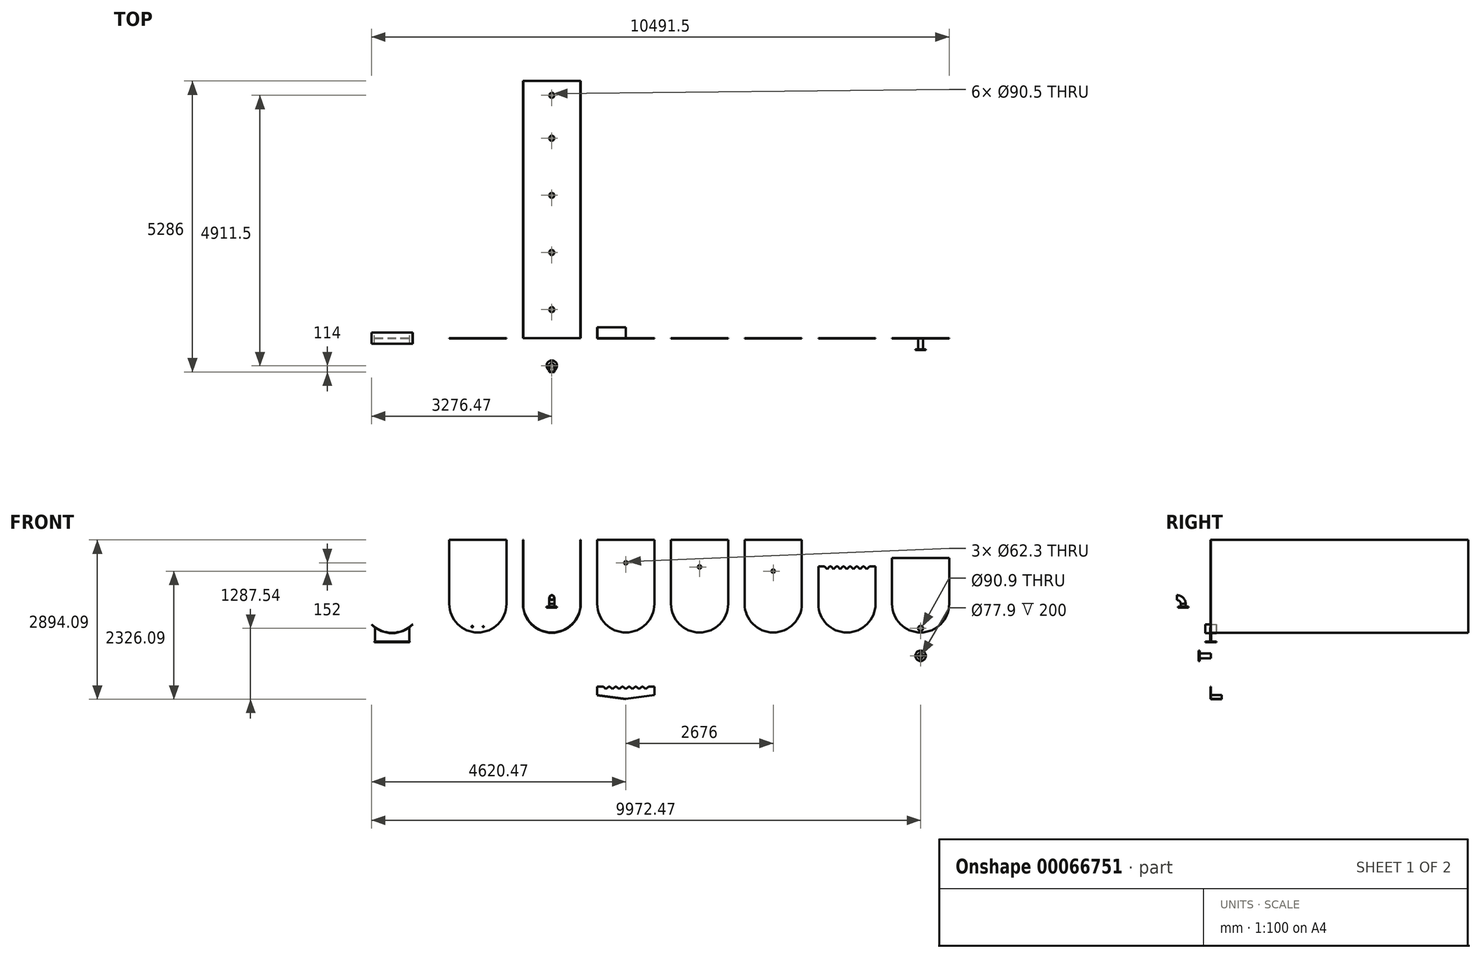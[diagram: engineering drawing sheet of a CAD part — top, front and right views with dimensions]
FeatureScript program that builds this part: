
annotation { "Feature Type Name" : "Feature", "Feature Type Description" : "" }
export const myFeature = defineFeature(function(context is Context, id is Id, definition is map)
    precondition{}
    {
        {
            assignVariable(context, id + "F0", {"name" : "A3", "anyValue" : 6});
        }
        {
            assignVariable(context, id + "F1", {"name" : "A20", "anyValue" : 18});
        }
        {
            assignVariable(context, id + "F2", {"name" : "A22", "anyValue" : 4});
        }
        {
            var Q0;
            Q0=qCreatedBy(makeId("Front.planeOp"),FACE);
            var sketch = newSketch(context, id + "F3", { "sketchPlane" : qUnion([Q0])});
            skLineSegment(sketch, "E0", {"start": v(-519, 1163) * mm, "end": v(-519, 0) * mm});
            skLineSegment(sketch, "E1", {"start": v(0, 0) * mm, "end": v(0, 1223.8) * mm, "construction": true});
            skLineSegment(sketch, "E2", {"start": v(-519, 1163) * mm, "end": v(-525, 1163) * mm});
            skLineSegment(sketch, "E3", {"start": v(-525, 1163) * mm, "end": v(-525, 0) * mm});
            skLineSegment(sketch, "E4.MirrorCS", {"start": v(519, 1163) * mm, "end": v(519, 0) * mm});
            skLineSegment(sketch, "E5.MirrorCS", {"start": v(519, 1163) * mm, "end": v(525, 1163) * mm});
            skLineSegment(sketch, "E6.MirrorCS", {"start": v(525, 1163) * mm, "end": v(525, 0) * mm});
            skArc(sketch, "E7", {"start": v(-519, 0) * mm, "mid": v(0, -519) * mm, "end": v(519, 0) * mm});
            skArc(sketch, "E8", {"start": v(-525, 0) * mm, "mid": v(0, -525) * mm, "end": v(525, 0) * mm});
            skLineSegment(sketch, "E9", {"start": v(-525, 1163) * mm, "end": v(-825, 1163) * mm, "construction": true});
            skLineSegment(sketch, "E10", {"start": v(-825, 1163) * mm, "end": v(-825, 0) * mm});
            skLineSegment(sketch, "E11", {"start": v(-825, 1163) * mm, "end": v(-1863, 1163) * mm});
            skLineSegment(sketch, "E12", {"start": v(-1863, 1163) * mm, "end": v(-1863, 0) * mm});
            skArc(sketch, "E13", {"start": v(-1863, 0) * mm, "mid": v(-1344, -519) * mm, "end": v(-825, 0) * mm});
            skLineSegment(sketch, "E14", {"start": v(525, 1163) * mm, "end": v(825, 1163) * mm, "construction": true});
            skLineSegment(sketch, "E15", {"start": v(825, 1163) * mm, "end": v(1863, 1163) * mm});
            skLineSegment(sketch, "E16", {"start": v(1863, 1163) * mm, "end": v(1863, 0) * mm});
            skLineSegment(sketch, "E17", {"start": v(825, 1163) * mm, "end": v(825, 0) * mm});
            skArc(sketch, "E18", {"start": v(825, 0) * mm, "mid": v(1344, -519) * mm, "end": v(1863, 0) * mm});
            skCircle(sketch, "E19", {"center": v(1344, 747) * mm, "radius": 31.15 * mm});
            skLineSegment(sketch, "E20", {"start": v(1863, 1163) * mm, "end": v(2163, 1163) * mm, "construction": true});
            skLineSegment(sketch, "E21", {"start": v(2163, 1163) * mm, "end": v(2163, 0) * mm});
            skLineSegment(sketch, "E22", {"start": v(2163, 1163) * mm, "end": v(3201, 1163) * mm});
            skLineSegment(sketch, "E23", {"start": v(3201, 1163) * mm, "end": v(3201, 0) * mm});
            skLineSegment(sketch, "E24", {"start": v(3201, 1163) * mm, "end": v(3501, 1163) * mm, "construction": true});
            skLineSegment(sketch, "E25", {"start": v(3501, 1163) * mm, "end": v(4539, 1163) * mm});
            skLineSegment(sketch, "E26", {"start": v(4539, 1163) * mm, "end": v(4539, 0) * mm});
            skLineSegment(sketch, "E27", {"start": v(3501, 1163) * mm, "end": v(3501, 0) * mm});
            skLineSegment(sketch, "E28", {"start": v(4539, 1163) * mm, "end": v(4839, 1163) * mm, "construction": true});
            skLineSegment(sketch, "E29", {"start": v(4839, 1163) * mm, "end": v(5877, 1163) * mm, "construction": true});
            skLineSegment(sketch, "E30", {"start": v(4839, 682.3) * mm, "end": v(4839, 0) * mm});
            skLineSegment(sketch, "E31", {"start": v(5877, 682.3) * mm, "end": v(5877, 0) * mm});
            skArc(sketch, "E32", {"start": v(2163, 0) * mm, "mid": v(2682, -519) * mm, "end": v(3201, 0) * mm});
            skArc(sketch, "E33", {"start": v(3501, 0) * mm, "mid": v(4020, -519) * mm, "end": v(4539, 0) * mm});
            skArc(sketch, "E34", {"start": v(4839, 0) * mm, "mid": v(5358, -519) * mm, "end": v(5877, 0) * mm});
            skCircle(sketch, "E35", {"center": v(2682, 671) * mm, "radius": 31.15 * mm});
            skCircle(sketch, "E36", {"center": v(4020, 595) * mm, "radius": 31.15 * mm});
            skCircle(sketch, "E37", {"center": v(5358, 520) * mm, "radius": 31.15 * mm, "construction": true});
            skLineSegment(sketch, "E38", {"start": v(-1863, 0) * mm, "end": v(-2901, 0) * mm, "construction": true});
            skLineSegment(sketch, "E39", {"start": v(-2901, 0) * mm, "end": v(-2901, -681) * mm, "construction": true});
            skLineSegment(sketch, "E40", {"start": v(-2901, 0) * mm, "end": v(-3272.23, -371.23) * mm, "construction": true});
            skArc(sketch, "E41", {"start": v(-3272.23, -371.23) * mm, "mid": v(-2901, -525) * mm, "end": v(-2529.77, -371.23) * mm});
            skArc(sketch, "E42.0", {"start": v(-3276.47, -375.47) * mm, "mid": v(-2901, -531) * mm, "end": v(-2525.53, -375.47) * mm});
            skLineSegment(sketch, "E43", {"start": v(-3272.23, -371.23) * mm, "end": v(-3276.47, -375.47) * mm});
            skLineSegment(sketch, "E44", {"start": v(-2529.77, -371.23) * mm, "end": v(-2525.53, -375.47) * mm});
            skLineSegment(sketch, "E45", {"start": v(-3220.22, -681) * mm, "end": v(-2581.78, -681) * mm});
            skLineSegment(sketch, "E46", {"start": v(-3220.22, -681) * mm, "end": v(-3220.22, -697) * mm});
            skLineSegment(sketch, "E47", {"start": v(-3220.22, -697) * mm, "end": v(-2581.78, -697) * mm});
            skLineSegment(sketch, "E48", {"start": v(-2581.78, -697) * mm, "end": v(-2581.78, -681) * mm});
            skLineSegment(sketch, "E49", {"start": v(-3211.47, -681) * mm, "end": v(-3211.47, -430.77) * mm});
            skLineSegment(sketch, "E50.MirrorCS", {"start": v(-2590.53, -681) * mm, "end": v(-2590.53, -430.77) * mm});
            skPoint(sketch, "E51.endSnap0", {"position": v(0, -519) * mm});
            skLineSegment(sketch, "E52", {"start": v(934, -1500) * mm, "end": v(984, -1550) * mm});
            skLineSegment(sketch, "E53", {"start": v(984, -1550) * mm, "end": v(984, -936.12) * mm, "construction": true});
            skLineSegment(sketch, "E54.MirrorCS", {"start": v(1034, -1500) * mm, "end": v(984, -1550) * mm});
            skLineSegment(sketch, "E55", {"start": v(934, -1500) * mm, "end": v(825, -1500) * mm});
            skLineSegment(sketch, "E56", {"start": v(1034, -1500) * mm, "end": v(1054, -1500) * mm});
            skLineSegment(sketch, "E57.1.0.0", {"start": v(1054, -1500) * mm, "end": v(1104, -1550) * mm});
            skLineSegment(sketch, "E57.1.0.1", {"start": v(1154, -1500) * mm, "end": v(1104, -1550) * mm});
            skLineSegment(sketch, "E57.1.0.2", {"start": v(1154, -1500) * mm, "end": v(1174, -1500) * mm});
            skLineSegment(sketch, "E57.2.0.0", {"start": v(1174, -1500) * mm, "end": v(1224, -1550) * mm});
            skLineSegment(sketch, "E57.2.0.1", {"start": v(1274, -1500) * mm, "end": v(1224, -1550) * mm});
            skLineSegment(sketch, "E57.2.0.2", {"start": v(1274, -1500) * mm, "end": v(1294, -1500) * mm});
            skLineSegment(sketch, "E57.3.0.0", {"start": v(1294, -1500) * mm, "end": v(1344, -1550) * mm});
            skLineSegment(sketch, "E57.3.0.1", {"start": v(1394, -1500) * mm, "end": v(1344, -1550) * mm});
            skLineSegment(sketch, "E57.3.0.2", {"start": v(1394, -1500) * mm, "end": v(1414, -1500) * mm});
            skLineSegment(sketch, "E57.4.0.0", {"start": v(1414, -1500) * mm, "end": v(1464, -1550) * mm});
            skLineSegment(sketch, "E57.4.0.1", {"start": v(1514, -1500) * mm, "end": v(1464, -1550) * mm});
            skLineSegment(sketch, "E57.4.0.2", {"start": v(1514, -1500) * mm, "end": v(1534, -1500) * mm});
            skLineSegment(sketch, "E57.5.0.0", {"start": v(1534, -1500) * mm, "end": v(1584, -1550) * mm});
            skLineSegment(sketch, "E57.5.0.1", {"start": v(1634, -1500) * mm, "end": v(1584, -1550) * mm});
            skLineSegment(sketch, "E57.5.0.2", {"start": v(1634, -1500) * mm, "end": v(1654, -1500) * mm});
            skLineSegment(sketch, "E57.6.0.0", {"start": v(1654, -1500) * mm, "end": v(1704, -1550) * mm});
            skLineSegment(sketch, "E57.6.0.1", {"start": v(1754, -1500) * mm, "end": v(1704, -1550) * mm});
            skLineSegment(sketch, "E57.6.0.2", {"start": v(1754, -1500) * mm, "end": v(1774, -1500) * mm});
            skLineSegment(sketch, "E57.direction1", {"start": v(984, -1550) * mm, "end": v(1104, -1550) * mm, "construction": true});
            skLineSegment(sketch, "E58", {"start": v(825, -1500) * mm, "end": v(825, -1656.25) * mm});
            skLineSegment(sketch, "E59", {"start": v(825, -1656.25) * mm, "end": v(1344, -1725.15) * mm});
            skLineSegment(sketch, "E60", {"start": v(1344, -1550) * mm, "end": v(1344, -1725.15) * mm, "construction": true});
            skLineSegment(sketch, "E61.MirrorCS", {"start": v(1863, -1656.25) * mm, "end": v(1344, -1725.15) * mm});
            skLineSegment(sketch, "E62.MirrorCS", {"start": v(1863, -1500) * mm, "end": v(1863, -1656.25) * mm});
            skLineSegment(sketch, "E63", {"start": v(1774, -1500) * mm, "end": v(1863, -1500) * mm});
            skCircle(sketch, "E64", {"center": v(1344, -1662.3) * mm, "radius": 31.15 * mm, "construction": true});
            skLineSegment(sketch, "E65", {"start": v(825.79, -1656.35) * mm, "end": v(825, -1662.3) * mm});
            skLineSegment(sketch, "E66", {"start": v(825, -1662.3) * mm, "end": v(1343.21, -1731.1) * mm});
            skLineSegment(sketch, "E67", {"start": v(1343.21, -1731.1) * mm, "end": v(1344, -1725.15) * mm});
            skLineSegment(sketch, "E68", {"start": v(825, -1656.25) * mm, "end": v(825, -1662.3) * mm, "construction": true});
            skLineSegment(sketch, "E69", {"start": v(4839, 682.3) * mm, "end": v(4948, 682.3) * mm});
            skLineSegment(sketch, "E70", {"start": v(4948, 682.3) * mm, "end": v(4998, 632.3) * mm});
            skLineSegment(sketch, "E71", {"start": v(4998, 632.3) * mm, "end": v(5048, 682.3) * mm});
            skLineSegment(sketch, "E72", {"start": v(5048, 682.3) * mm, "end": v(5068, 682.3) * mm});
            skLineSegment(sketch, "E73", {"start": v(4998, 632.3) * mm, "end": v(4998, 1117.93) * mm, "construction": true});
            skLineSegment(sketch, "E74.1.0.0", {"start": v(5068, 682.3) * mm, "end": v(5118, 632.3) * mm});
            skLineSegment(sketch, "E74.1.0.1", {"start": v(5118, 632.3) * mm, "end": v(5168, 682.3) * mm});
            skLineSegment(sketch, "E74.1.0.2", {"start": v(5168, 682.3) * mm, "end": v(5188, 682.3) * mm});
            skLineSegment(sketch, "E74.2.0.0", {"start": v(5188, 682.3) * mm, "end": v(5238, 632.3) * mm});
            skLineSegment(sketch, "E74.2.0.1", {"start": v(5238, 632.3) * mm, "end": v(5288, 682.3) * mm});
            skLineSegment(sketch, "E74.2.0.2", {"start": v(5288, 682.3) * mm, "end": v(5308, 682.3) * mm});
            skLineSegment(sketch, "E74.3.0.0", {"start": v(5308, 682.3) * mm, "end": v(5358, 632.3) * mm});
            skLineSegment(sketch, "E74.3.0.1", {"start": v(5358, 632.3) * mm, "end": v(5408, 682.3) * mm});
            skLineSegment(sketch, "E74.3.0.2", {"start": v(5408, 682.3) * mm, "end": v(5428, 682.3) * mm});
            skLineSegment(sketch, "E74.4.0.0", {"start": v(5428, 682.3) * mm, "end": v(5478, 632.3) * mm});
            skLineSegment(sketch, "E74.4.0.1", {"start": v(5478, 632.3) * mm, "end": v(5528, 682.3) * mm});
            skLineSegment(sketch, "E74.4.0.2", {"start": v(5528, 682.3) * mm, "end": v(5548, 682.3) * mm});
            skLineSegment(sketch, "E74.5.0.0", {"start": v(5548, 682.3) * mm, "end": v(5598, 632.3) * mm});
            skLineSegment(sketch, "E74.5.0.1", {"start": v(5598, 632.3) * mm, "end": v(5648, 682.3) * mm});
            skLineSegment(sketch, "E74.5.0.2", {"start": v(5648, 682.3) * mm, "end": v(5668, 682.3) * mm});
            skLineSegment(sketch, "E74.6.0.0", {"start": v(5668, 682.3) * mm, "end": v(5718, 632.3) * mm});
            skLineSegment(sketch, "E74.6.0.1", {"start": v(5718, 632.3) * mm, "end": v(5768, 682.3) * mm});
            skLineSegment(sketch, "E74.6.0.2", {"start": v(5768, 682.3) * mm, "end": v(5788, 682.3) * mm});
            skLineSegment(sketch, "E74.direction1", {"start": v(4998, 632.3) * mm, "end": v(5118, 632.3) * mm, "construction": true});
            skLineSegment(sketch, "E75", {"start": v(5788, 682.3) * mm, "end": v(5877, 682.3) * mm});
            skLineSegment(sketch, "E76", {"start": v(5358, 520) * mm, "end": v(5358, 632.3) * mm, "construction": true});
            skLineSegment(sketch, "E77", {"start": v(5877, 1163) * mm, "end": v(6177, 1163) * mm, "construction": true});
            skLineSegment(sketch, "E78", {"start": v(6177, 1163) * mm, "end": v(7215, 1163) * mm, "construction": true});
            skLineSegment(sketch, "E79", {"start": v(7215, 832.3) * mm, "end": v(7215, 0) * mm});
            skLineSegment(sketch, "E80", {"start": v(6177, 832.3) * mm, "end": v(6177, 0) * mm});
            skArc(sketch, "E81", {"start": v(6177, 0) * mm, "mid": v(6696, -519) * mm, "end": v(7215, 0) * mm});
            skLineSegment(sketch, "E82", {"start": v(6177, 832.3) * mm, "end": v(7215, 832.3) * mm});
            skCircle(sketch, "E83", {"center": v(6696, -443.55) * mm, "radius": 45.45 * mm});
            skCircle(sketch, "E84", {"center": v(6696, -943.55) * mm, "radius": 44.45 * mm});
            skCircle(sketch, "E85", {"center": v(6696, -943.55) * mm, "radius": 38.95 * mm});
            skCircle(sketch, "E86", {"center": v(-1444, -413.07) * mm, "radius": 14 * mm});
            skCircle(sketch, "E87", {"center": v(-1244, -413.07) * mm, "radius": 9.5 * mm});
            skLineSegment(sketch, "E88", {"start": v(-1344, 0) * mm, "end": v(-1344, -413.07) * mm, "construction": true});
            skLineSegment(sketch, "E89", {"start": v(-1444, -413.07) * mm, "end": v(-1244, -413.07) * mm, "construction": true});
            skSolve(sketch);
        }
        {
            assignVariable(context, id + "F4", {"name" : "A24", "anyValue" : 4672});
        }
        {
            var Q0;
            Q0=makeQuery(id+"F3.imprint","IMPRINT",FACE,{"disambiguationData":[TD([[makeQuery(id+"F3.imprint","IMPRINT",EDGE,{"derivedFrom":sQuery(id+"F3.wireOp",EDGE,"E0")}),-1.0]])]});
            extrude(context, id + "F5", {"entities" : qUnion([Q0]), "oppositeDirection" : true, "depth" : (getVariable(context, 'A24')) * mm});
        }
        {
            var Q0;
            Q0=makeQuery(id+"F3.imprint","IMPRINT",FACE,{"disambiguationData":[TD([[makeQuery(id+"F3.imprint","IMPRINT",EDGE,{"derivedFrom":sQuery(id+"F3.wireOp",EDGE,"E10")}),-1.0]])]});
            extrude(context, id + "F6", {"entities" : qUnion([Q0]), "depth" : (getVariable(context, 'A3')) * mm});
        }
        {
            var Q0;
            Q0=makeQuery(id+"F3.imprint","IMPRINT",FACE,{"disambiguationData":[TD([[makeQuery(id+"F3.imprint","IMPRINT",EDGE,{"derivedFrom":sQuery(id+"F3.wireOp",EDGE,"E15")}),-1.0]])]});
            extrude(context, id + "F7", {"entities" : qUnion([Q0]), "depth" : (getVariable(context, 'A3')) * mm});
        }
        {
            var Q0;
            Q0=makeQuery(id+"F3.imprint","IMPRINT",FACE,{"disambiguationData":[TD([[makeQuery(id+"F3.imprint","IMPRINT",EDGE,{"derivedFrom":sQuery(id+"F3.wireOp",EDGE,"E21")}),1.0]])]});
            extrude(context, id + "F8", {"entities" : qUnion([Q0]), "depth" : (getVariable(context, 'A3')) * mm});
        }
        {
            var Q0;
            Q0=makeQuery(id+"F3.imprint","IMPRINT",FACE,{"disambiguationData":[TD([[makeQuery(id+"F3.imprint","IMPRINT",EDGE,{"derivedFrom":sQuery(id+"F3.wireOp",EDGE,"E25")}),-1.0]])]});
            extrude(context, id + "F9", {"entities" : qUnion([Q0]), "depth" : (getVariable(context, 'A3')) * mm});
        }
        {
            var Q0;
            Q0=makeQuery(id+"F3.imprint","IMPRINT",FACE,{"disambiguationData":[TD([[makeQuery(id+"F3.imprint","IMPRINT",EDGE,{"derivedFrom":sQuery(id+"F3.wireOp",EDGE,"E30")}),1.0]])]});
            extrude(context, id + "F10", {"entities" : qUnion([Q0]), "depth" : (getVariable(context, 'A3')) * mm});
        }
        {
            var Q0;
            Q0=makeQuery(id+"F3.imprint","IMPRINT",FACE,{"disambiguationData":[TD([[makeQuery(id+"F3.imprint","IMPRINT",EDGE,{"derivedFrom":sQuery(id+"F3.wireOp",EDGE,"E79")}),-1.0]])]});
            extrude(context, id + "F11", {"entities" : qUnion([Q0]), "depth" : (getVariable(context, 'A3')) * mm});
        }
        {
            var Q0;
            Q0=makeQuery(id+"F3.imprint","IMPRINT",FACE,{"disambiguationData":[TD([[makeQuery(id+"F3.imprint","IMPRINT",EDGE,{"derivedFrom":sQuery(id+"F3.wireOp",EDGE,"E52")}),-1.0]])]});
            extrude(context, id + "F12", {"entities" : qUnion([Q0]), "depth" : (getVariable(context, 'A3')) * mm});
        }
        {
            var Q0;
            {var subQ2=sQuery(id+"F3.wireOp",EDGE,"E65");Q0=makeQuery(id+"F3.imprint","IMPRINT",FACE,{"disambiguationData":[TD([[makeQuery(id+"F3.imprint","IMPRINT",EDGE,{"derivedFrom":subQ2}),1.0]])]});}
            extrude(context, id + "F13", {"entities" : qUnion([Q0]), "operationType" : NewBodyOperationType.ADD, "oppositeDirection" : true, "depth" : 200 * mm});
        }
        {
            var Q0;
            Q0=makeQuery(id+"F3.imprint","IMPRINT",FACE,{"disambiguationData":[TD([[makeQuery(id+"F3.imprint","IMPRINT",EDGE,{"derivedFrom":sQuery(id+"F3.wireOp",EDGE,"E41")}),-1.0]])]});
            extrude(context, id + "F14", {"entities" : qUnion([Q0]), "depth" : 200 * mm, "symmetric" : true});
        }
        {
            var Q0;
            {var subQ0=sQuery(id+"F3.wireOp",EDGE,"E49");Q0=makeQuery(id+"F3.imprint","IMPRINT",FACE,{"disambiguationData":[TD([[makeQuery(id+"F3.imprint","IMPRINT",EDGE,{"derivedFrom":subQ0}),-1.0]])]});}
            extrude(context, id + "F15", {"entities" : qUnion([Q0]), "operationType" : NewBodyOperationType.ADD, "depth" : 16 * mm, "symmetric" : true});
        }
        {
            var Q0;
            {var subQ0=sQuery(id+"F3.wireOp",EDGE,"E46");Q0=makeQuery(id+"F3.imprint","IMPRINT",FACE,{"disambiguationData":[TD([[makeQuery(id+"F3.imprint","IMPRINT",EDGE,{"derivedFrom":subQ0}),1.0]])]});}
            extrude(context, id + "F16", {"entities" : qUnion([Q0]), "operationType" : NewBodyOperationType.ADD, "depth" : 200 * mm, "symmetric" : true});
        }
        {
            var Q0;
            Q0=makeQuery(id+"F3.imprint","IMPRINT",FACE,{"disambiguationData":[TD([[makeQuery(id+"F3.imprint","IMPRINT",EDGE,{"derivedFrom":sQuery(id+"F3.wireOp",EDGE,"E84")}),1.0]])]});
            extrude(context, id + "F17", {"entities" : qUnion([Q0]), "depth" : 200 * mm});
        }
        {
            var Q0;
            Q0=makeQuery(id+"F17.opExtrude","CAP_FACE",FACE,{"disambiguationData":[OSD([sQuery(id+"F3.wireOp",EDGE,"E84"),sQuery(id+"F3.wireOp",EDGE,"E85")])],"isStart":false});
            var sketch = newSketch(context, id + "F18", { "sketchPlane" : qUnion([Q0])});
            skCircle(sketch, "E90", {"center": v(6696, -943.55) * mm, "radius": 45.25 * mm});
            skCircle(sketch, "E91", {"center": v(6696, -943.55) * mm, "radius": 95 * mm});
            skCircle(sketch, "E92", {"center": v(6696, -943.55) * mm, "radius": 75 * mm, "construction": true});
            skCircle(sketch, "E93", {"center": v(6696, -868.55) * mm, "radius": 9 * mm});
            skSolve(sketch);
        }
        {
            var Q0;
            Q0=makeQuery(id+"F18.imprint","IMPRINT",FACE,{"disambiguationData":[TD([[makeQuery(id+"F18.imprint","IMPRINT",EDGE,{"derivedFrom":sQuery(id+"F18.wireOp",EDGE,"E90")}),-1.0]])]});
            extrude(context, id + "F19", {"entities" : qUnion([Q0]), "depth" : (getVariable(context, 'A20')) * mm});
        }
        {
            var Q0;
            Q0=makeQuery(id+"F19.opExtrude","SWEPT_FACE",FACE,{"disambiguationData":[OSD([sQuery(id+"F18.wireOp",EDGE,"E93")])]});
            var Q1;
            Q1=makeQuery(id+"F19.opExtrude","CAP_EDGE",EDGE,{"disambiguationData":[OSD([sQuery(id+"F18.wireOp",EDGE,"E90")])],"isStart":false});
            circularPattern(context, id + "F20", {"faces" : qUnion([Q0]), "axis" : qUnion([Q1]), "angle" : 360 * degree, "instanceCount" : getVariable(context, 'A22'), "equalSpace" : true, "patternType" : PatternType.FACE});
        }
        {
            assignVariable(context, id + "F21", {"name" : "A30", "anyValue" : 18});
        }
        {
            assignVariable(context, id + "F22", {"name" : "A32", "anyValue" : 4});
        }
        {
            var Q0;
            Q0=qCreatedBy(makeId("Top.planeOp"),FACE);
            var sketch = newSketch(context, id + "F23", { "sketchPlane" : qUnion([Q0])});
            skCircle(sketch, "E94", {"center": v(0, 519) * mm, "radius": 45.25 * mm});
            skCircle(sketch, "E95.0.1.0", {"center": v(0, 1557) * mm, "radius": 45.25 * mm});
            skCircle(sketch, "E95.0.2.0", {"center": v(0, 2595) * mm, "radius": 45.25 * mm});
            skCircle(sketch, "E95.0.3.0", {"center": v(0, 3633) * mm, "radius": 45.25 * mm});
            skLineSegment(sketch, "E95.direction1", {"start": v(0, 519) * mm, "end": v(25, 519) * mm, "construction": true});
            skLineSegment(sketch, "E95.direction2", {"start": v(0, 519) * mm, "end": v(0, 1557) * mm, "construction": true});
            skCircle(sketch, "E96", {"center": v(0, 4411.5) * mm, "radius": 45.25 * mm});
            skSolve(sketch);
        }
        {
            var Q0;
            Q0 = qSketchRegion(id + "F23", true);
            extrude(context, id + "F24", {"entities" : qUnion([Q0]), "operationType" : NewBodyOperationType.REMOVE, "endBound" : BoundingType.THROUGH_ALL, "oppositeDirection" : true, "depth" : 25 * mm});
        }
        {
            var Q0;
            Q0=qCreatedBy(makeId("Top.planeOp"),FACE);
            var sketch = newSketch(context, id + "F25", { "sketchPlane" : qUnion([Q0])});
            skCircle(sketch, "E97", {"center": v(0, -500) * mm, "radius": 44.45 * mm});
            skCircle(sketch, "E98", {"center": v(0, -500) * mm, "radius": 38.95 * mm});
            skSolve(sketch);
        }
        {
            var Q0;
            Q0=makeQuery(id+"F25.imprint","IMPRINT",FACE,{"disambiguationData":[TD([[makeQuery(id+"F25.imprint","IMPRINT",EDGE,{"derivedFrom":sQuery(id+"F25.wireOp",EDGE,"E97")}),1.0]])]});
            extrude(context, id + "F26", {"entities" : qUnion([Q0]), "oppositeDirection" : true, "depth" : 50 * mm});
        }
        {
            var Q0;
            Q0=makeQuery(id+"F26.opExtrude","CAP_FACE",FACE,{"disambiguationData":[OSD([sQuery(id+"F25.wireOp",EDGE,"E97"),sQuery(id+"F25.wireOp",EDGE,"E98")])],"isStart":false});
            var sketch = newSketch(context, id + "F27", { "sketchPlane" : qUnion([Q0])});
            skCircle(sketch, "E99", {"center": v(0, 500) * mm, "radius": 95 * mm});
            skCircle(sketch, "E100", {"center": v(0, 500) * mm, "radius": 45.25 * mm});
            skCircle(sketch, "E101", {"center": v(0, 500) * mm, "radius": 75 * mm, "construction": true});
            skCircle(sketch, "E102", {"center": v(0, 575) * mm, "radius": 9 * mm});
            skSolve(sketch);
        }
        {
            var Q0;
            Q0=makeQuery(id+"F27.imprint","IMPRINT",FACE,{"disambiguationData":[TD([[makeQuery(id+"F27.imprint","IMPRINT",EDGE,{"derivedFrom":sQuery(id+"F27.wireOp",EDGE,"E99")}),1.0]])]});
            extrude(context, id + "F28", {"entities" : qUnion([Q0]), "depth" : (getVariable(context, 'A30')) * mm});
        }
        {
            var Q0;
            Q0=makeQuery(id+"F28.opExtrude","SWEPT_BODY",BODY,{"disambiguationData":[OSD([sQuery(id+"F27.wireOp",EDGE,"E99"),sQuery(id+"F27.wireOp",EDGE,"E100"),sQuery(id+"F27.wireOp",EDGE,"E102")])]});
            var Q1;
            Q1=makeQuery(id+"F28.opExtrude","SWEPT_FACE",FACE,{"disambiguationData":[OSD([sQuery(id+"F27.wireOp",EDGE,"E102")])]});
            var Q2;
            Q2=makeQuery(id+"F28.opExtrude","CAP_EDGE",EDGE,{"disambiguationData":[OSD([sQuery(id+"F27.wireOp",EDGE,"E100")])],"isStart":true});
            circularPattern(context, id + "F29", {"patternType" : PatternType.FACE, "faces" : qUnion([Q1]), "axis" : qUnion([Q2]), "angle" : 360 * degree, "instanceCount" : getVariable(context, 'A32'), "equalSpace" : true});
        }
        {
            var Q0;
            Q0=qCreatedBy(makeId("Right.planeOp"),FACE);
            var sketch = newSketch(context, id + "F30", { "sketchPlane" : qUnion([Q0])});
            skLineSegment(sketch, "E103", {"start": v(-500, 0) * mm, "end": v(-614, 0) * mm, "construction": true});
            skLineSegment(sketch, "E104", {"start": v(-614, 0) * mm, "end": v(-614, 114) * mm, "construction": true});
            skArc(sketch, "E105", {"start": v(-500, 0) * mm, "mid": v(-533.39, 80.61) * mm, "end": v(-614, 114) * mm});
            skSolve(sketch);
        }
        {
            var Q0;
            Q0=makeQuery(id+"F25.imprint","IMPRINT",FACE,{"disambiguationData":[TD([[makeQuery(id+"F25.imprint","IMPRINT",EDGE,{"derivedFrom":sQuery(id+"F25.wireOp",EDGE,"E97")}),1.0]])]});
            var Q1;
            Q1=sQuery(id+"F30.wireOp",EDGE,"E105");
            sweep(context, id + "F31", {"profiles" : qUnion([Q0]), "path" : qUnion([Q1])});
        }
    });
